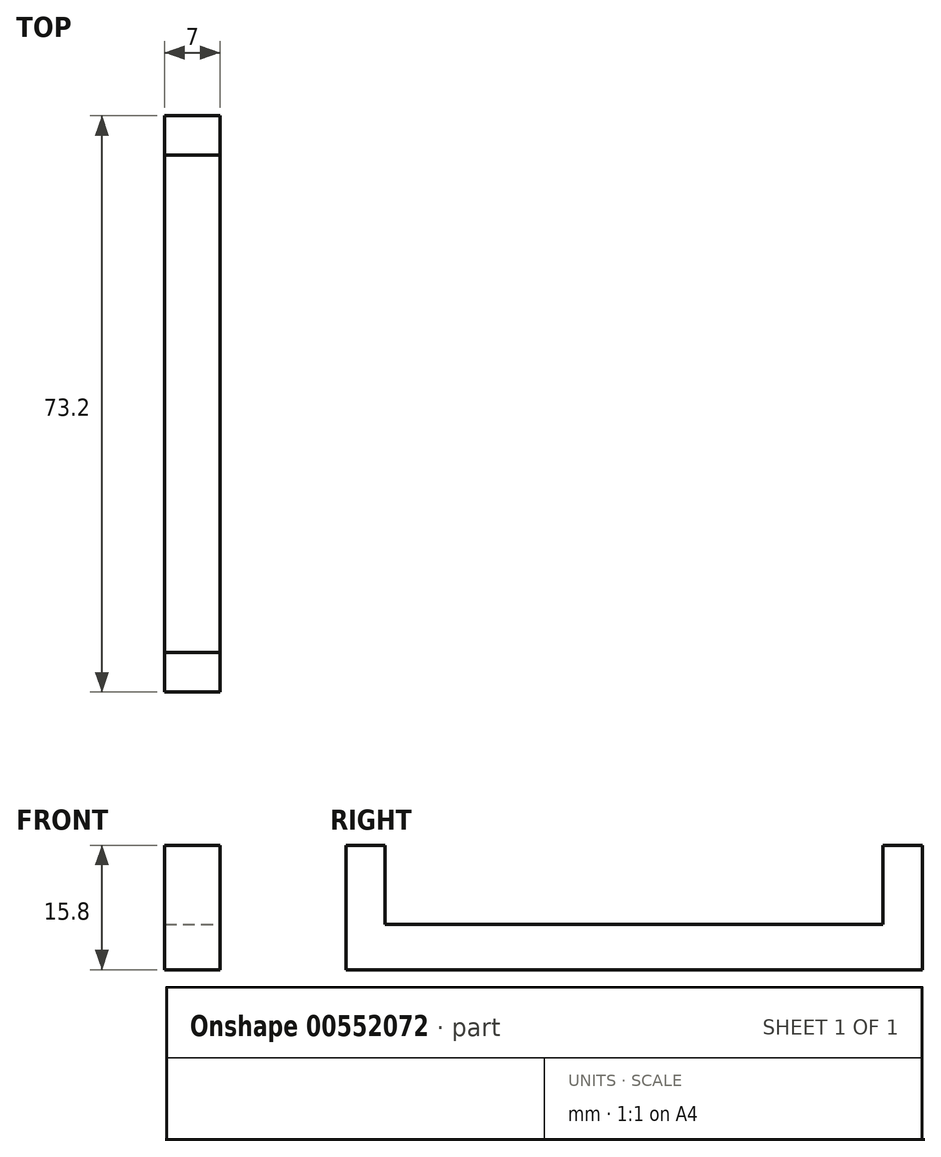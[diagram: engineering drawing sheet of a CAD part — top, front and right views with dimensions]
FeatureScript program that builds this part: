
annotation { "Feature Type Name" : "Feature", "Feature Type Description" : "" }
export const myFeature = defineFeature(function(context is Context, id is Id, definition is map)
    precondition{}
    {
        {
            var Q0;
            Q0=qCreatedBy(makeId("Top.planeOp"),FACE);
            var sketch = newSketch(context, id + "F0", { "sketchPlane" : qUnion([Q0])});
            skLineSegment(sketch, "E0.bottom", {"start": v(3.5, -36.6) * mm, "end": v(-3.5, -36.6) * mm});
            skLineSegment(sketch, "E0.top", {"start": v(3.5, 36.6) * mm, "end": v(-3.5, 36.6) * mm});
            skLineSegment(sketch, "E0.left", {"start": v(3.5, -36.6) * mm, "end": v(3.5, 36.6) * mm});
            skLineSegment(sketch, "E0.right", {"start": v(-3.5, -36.6) * mm, "end": v(-3.5, 36.6) * mm});
            skPoint(sketch, "E0.middle", {"position": v(0, 0) * mm});
            skSolve(sketch);
        }
        {
            var Q0;
            Q0=qSketchRegion(id+"F0",true);
            extrude(context, id + "F1", {"entities" : qUnion([Q0]), "depth" : 5.8 * mm, "offsetDistance" : 25 * mm});
        }
        {
            var Q0;
            Q0=makeQuery(id+"F1.opExtrude","CAP_FACE",FACE,{"disambiguationData":[OSD([sQuery(id+"F0.wireOp",EDGE,"E0.bottom"),sQuery(id+"F0.wireOp",EDGE,"E0.top"),sQuery(id+"F0.wireOp",EDGE,"E0.left"),sQuery(id+"F0.wireOp",EDGE,"E0.right")])],"isStart":false});
            var sketch = newSketch(context, id + "F2", { "sketchPlane" : qUnion([Q0])});
            skLineSegment(sketch, "E1.bottom", {"start": v(-3.5, 36.6) * mm, "end": v(3.5, 36.6) * mm});
            skLineSegment(sketch, "E1.top", {"start": v(-3.5, 31.6) * mm, "end": v(3.5, 31.6) * mm});
            skLineSegment(sketch, "E1.left", {"start": v(-3.5, 36.6) * mm, "end": v(-3.5, 31.6) * mm});
            skLineSegment(sketch, "E1.right", {"start": v(3.5, 36.6) * mm, "end": v(3.5, 31.6) * mm});
            skLineSegment(sketch, "E2", {"start": v(0, 0) * mm, "end": v(-36.95, 0) * mm, "construction": true});
            skLineSegment(sketch, "E3.MirrorCS", {"start": v(3.5, -36.6) * mm, "end": v(3.5, -31.6) * mm});
            skLineSegment(sketch, "E4.MirrorCS", {"start": v(-3.5, -36.6) * mm, "end": v(-3.5, -31.6) * mm});
            skLineSegment(sketch, "E5.MirrorCS", {"start": v(-3.5, -36.6) * mm, "end": v(3.5, -36.6) * mm});
            skLineSegment(sketch, "E6.MirrorCS", {"start": v(-3.5, -31.6) * mm, "end": v(3.5, -31.6) * mm});
            skSolve(sketch);
        }
        {
            var Q0;
            Q0=qSketchRegion(id+"F2",true);
            extrude(context, id + "F3", {"entities" : qUnion([Q0]), "operationType" : NewBodyOperationType.ADD, "depth" : 10 * mm, "offsetDistance" : 25 * mm});
        }
    });
